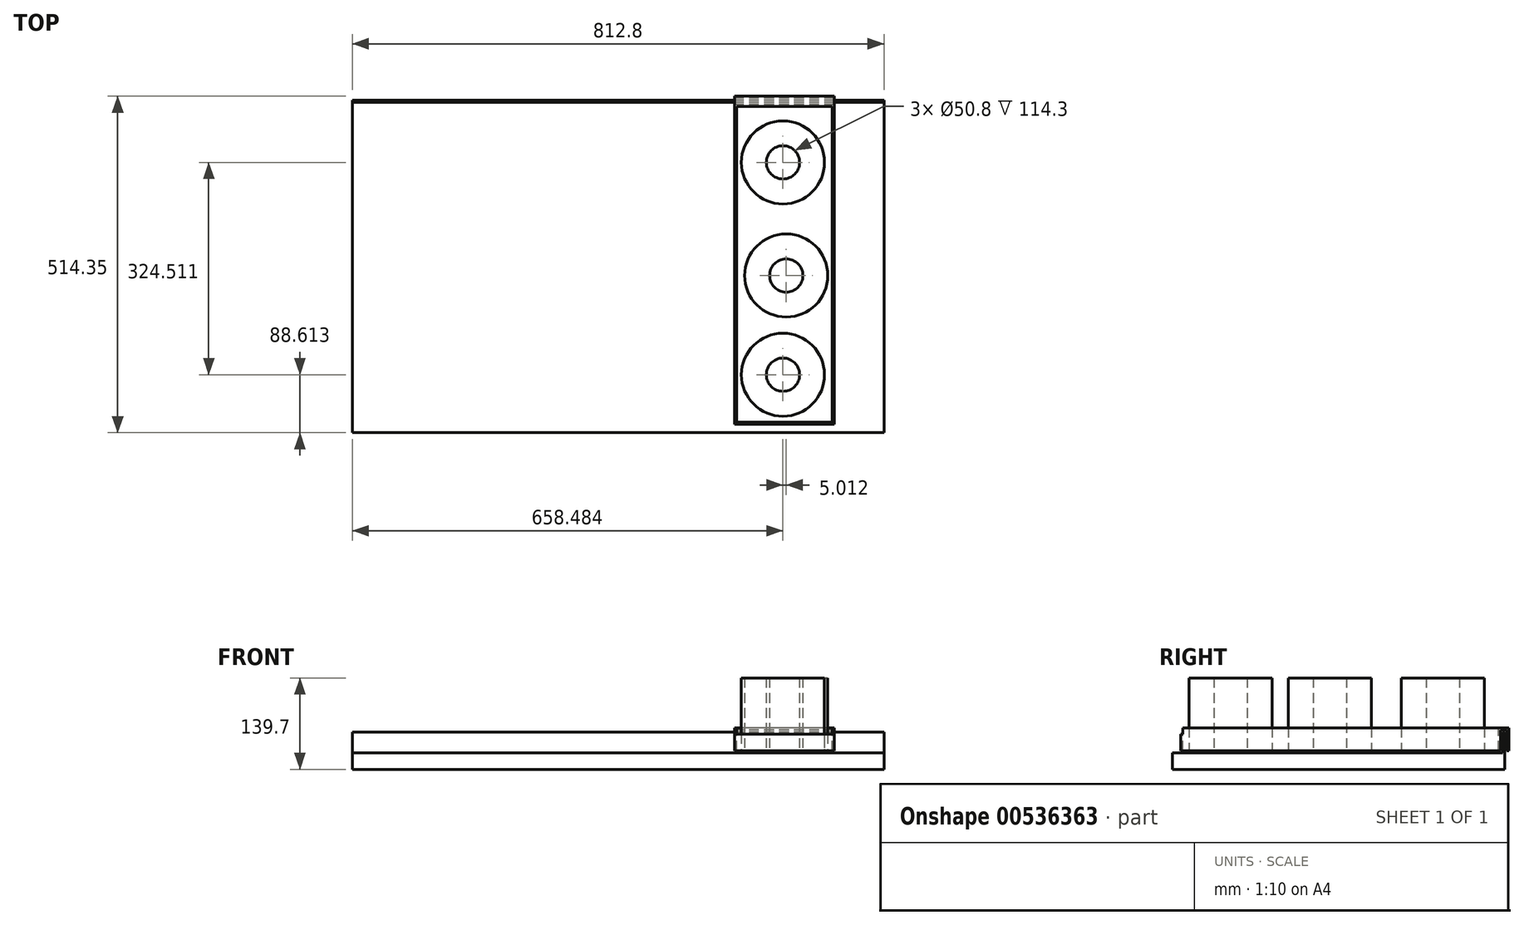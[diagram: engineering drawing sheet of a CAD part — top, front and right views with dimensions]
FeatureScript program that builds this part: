
annotation { "Feature Type Name" : "Feature", "Feature Type Description" : "" }
export const myFeature = defineFeature(function(context is Context, id is Id, definition is map)
    precondition{}
    {
        {
            var Q0;
            Q0=qCreatedBy(makeId("Top.planeOp"),FACE);
            var sketch = newSketch(context, id + "F0", { "sketchPlane" : qUnion([Q0])});
            skLineSegment(sketch, "E0.bottom", {"start": v(-406.4, 254) * mm, "end": v(406.4, 254) * mm});
            skLineSegment(sketch, "E0.top", {"start": v(-406.4, -254) * mm, "end": v(406.4, -254) * mm});
            skLineSegment(sketch, "E0.left", {"start": v(-406.4, 254) * mm, "end": v(-406.4, -254) * mm});
            skLineSegment(sketch, "E0.right", {"start": v(406.4, 254) * mm, "end": v(406.4, -254) * mm});
            skPoint(sketch, "E0.middle", {"position": v(0, 0) * mm});
            skSolve(sketch);
        }
        {
            var Q0;
            Q0 = qSketchRegion(id + "F0", true);
            extrude(context, id + "F1", {"entities" : qUnion([Q0]), "oppositeDirection" : true, "depth" : 25.4 * mm, "offsetDistance" : 25.4 * mm});
        }
        {
            var Q0;
            Q0=qCreatedBy(makeId("Right.planeOp"),FACE);
            var sketch = newSketch(context, id + "F2", { "sketchPlane" : qUnion([Q0])});
            skLineSegment(sketch, "E1.bottom", {"start": v(254, 0) * mm, "end": v(250.83, 0) * mm});
            skLineSegment(sketch, "E1.top", {"start": v(254, 31.75) * mm, "end": v(250.83, 31.75) * mm});
            skLineSegment(sketch, "E1.left", {"start": v(254, 0) * mm, "end": v(254, 31.75) * mm});
            skLineSegment(sketch, "E1.right", {"start": v(250.83, 0) * mm, "end": v(250.83, 31.75) * mm});
            skSolve(sketch);
        }
        {
            var Q0;
            Q0 = qSketchRegion(id + "F2", true);
            extrude(context, id + "F3", {"entities" : qUnion([Q0]), "operationType" : NewBodyOperationType.ADD, "endBound" : BoundingType.SYMMETRIC, "depth" : 812.8 * mm, "offsetDistance" : 25.4 * mm});
        }
        {
            var Q0;
            Q0=qCreatedBy(makeId("Right.planeOp"),FACE);
            cPlane(context, id + "F4", {"entities" : qUnion([Q0]), "cplaneType" : CPlaneType.OFFSET, "offset" : 254 * mm, "width" : 152.4 * mm, "height" : 152.4 * mm});
        }
        {
            var Q0;
            Q0=qCreatedBy(id+"F4.planeOp",FACE);
            var sketch = newSketch(context, id + "F5", { "sketchPlane" : qUnion([Q0])});
            skLineSegment(sketch, "E2", {"start": v(247.65, 3.18) * mm, "end": v(244.49, 3.18) * mm});
            skLineSegment(sketch, "E3", {"start": v(244.49, 3.18) * mm, "end": v(244.49, 38.1) * mm});
            skLineSegment(sketch, "E4", {"start": v(244.49, 38.1) * mm, "end": v(260.35, 38.1) * mm});
            skLineSegment(sketch, "E5", {"start": v(260.35, 38.1) * mm, "end": v(260.35, 3.17) * mm});
            skLineSegment(sketch, "E6", {"start": v(260.35, 3.17) * mm, "end": v(257.18, 3.17) * mm});
            skLineSegment(sketch, "E7", {"start": v(257.18, 3.17) * mm, "end": v(257.18, 34.92) * mm});
            skLineSegment(sketch, "E8", {"start": v(257.18, 34.92) * mm, "end": v(247.65, 34.92) * mm});
            skLineSegment(sketch, "E9", {"start": v(247.65, 34.92) * mm, "end": v(247.65, 3.18) * mm});
            skSolve(sketch);
        }
        {
            var Q0;
            Q0 = qSketchRegion(id + "F5", true);
            extrude(context, id + "F6", {"entities" : qUnion([Q0]), "endBound" : BoundingType.SYMMETRIC, "depth" : 152.4 * mm, "offsetDistance" : 25.4 * mm});
        }
        {
            var Q0;
            Q0=makeQuery(id+"F6.opExtrude","SWEPT_FACE",FACE,{"disambiguationData":[OSD([sQuery(id+"F5.wireOp",EDGE,"E3")])]});
            var sketch = newSketch(context, id + "F7", { "sketchPlane" : qUnion([Q0])});
            skLineSegment(sketch, "E10.bottom", {"start": v(177.8, 3.18) * mm, "end": v(180.98, 3.18) * mm});
            skLineSegment(sketch, "E10.top", {"start": v(177.8, 38.1) * mm, "end": v(180.98, 38.1) * mm});
            skLineSegment(sketch, "E10.left", {"start": v(177.8, 3.18) * mm, "end": v(177.8, 38.1) * mm});
            skLineSegment(sketch, "E10.right", {"start": v(180.98, 3.18) * mm, "end": v(180.98, 38.1) * mm});
            skLineSegment(sketch, "E11.bottom", {"start": v(330.2, 3.18) * mm, "end": v(327.03, 3.18) * mm});
            skLineSegment(sketch, "E11.top", {"start": v(330.2, 38.1) * mm, "end": v(327.03, 38.1) * mm});
            skLineSegment(sketch, "E11.left", {"start": v(330.2, 3.18) * mm, "end": v(330.2, 38.1) * mm});
            skLineSegment(sketch, "E11.right", {"start": v(327.03, 3.18) * mm, "end": v(327.03, 38.1) * mm});
            skSolve(sketch);
        }
        {
            var Q0;
            Q0 = qSketchRegion(id + "F7", true);
            extrude(context, id + "F8", {"entities" : qUnion([Q0]), "operationType" : NewBodyOperationType.ADD, "depth" : 482.6 * mm, "offsetDistance" : 25.4 * mm});
        }
        {
            var Q0;
            Q0=makeQuery(id+"F8.opExtrude","CAP_FACE",FACE,{"disambiguationData":[OSD([sQuery(id+"F7.wireOp",EDGE,"E10.bottom"),sQuery(id+"F7.wireOp",EDGE,"E10.top"),sQuery(id+"F7.wireOp",EDGE,"E10.left"),sQuery(id+"F7.wireOp",EDGE,"E10.right")])],"isStart":false});
            var sketch = newSketch(context, id + "F9", { "sketchPlane" : qUnion([Q0])});
            skLineSegment(sketch, "E12.bottom", {"start": v(177.8, 3.18) * mm, "end": v(330.2, 3.18) * mm});
            skLineSegment(sketch, "E12.top", {"start": v(177.8, 28.58) * mm, "end": v(330.2, 28.58) * mm});
            skLineSegment(sketch, "E12.left", {"start": v(177.8, 3.18) * mm, "end": v(177.8, 28.58) * mm});
            skLineSegment(sketch, "E12.right", {"start": v(330.2, 3.18) * mm, "end": v(330.2, 28.58) * mm});
            skSolve(sketch);
        }
        {
            var Q0;
            Q0 = qSketchRegion(id + "F9", true);
            extrude(context, id + "F10", {"entities" : qUnion([Q0]), "operationType" : NewBodyOperationType.ADD, "depth" : 3.17 * mm, "offsetDistance" : 25.4 * mm});
        }
        {
            var Q0;
            Q0=makeQuery(id+"F1.opExtrude","CAP_FACE",FACE,{"disambiguationData":[OSD([sQuery(id+"F0.wireOp",EDGE,"E0.bottom"),sQuery(id+"F0.wireOp",EDGE,"E0.top"),sQuery(id+"F0.wireOp",EDGE,"E0.left"),sQuery(id+"F0.wireOp",EDGE,"E0.right")])],"isStart":true});
            var sketch = newSketch(context, id + "F11", { "sketchPlane" : qUnion([Q0])});
            skCircle(sketch, "E13", {"center": v(252.08, 159.12) * mm, "radius": 63.5 * mm});
            skCircle(sketch, "E14", {"center": v(257.1, -13.78) * mm, "radius": 63.5 * mm});
            skCircle(sketch, "E15", {"center": v(257.1, -13.78) * mm, "radius": 25.4 * mm});
            skCircle(sketch, "E16", {"center": v(252.08, 159.12) * mm, "radius": 25.4 * mm});
            skCircle(sketch, "E17", {"center": v(252.08, -165.39) * mm, "radius": 63.5 * mm});
            skCircle(sketch, "E18", {"center": v(252.08, -165.39) * mm, "radius": 25.4 * mm});
            skSolve(sketch);
        }
        {
            var Q0;
            Q0 = qSketchRegion(id + "F11", true);
            extrude(context, id + "F12", {"entities" : qUnion([Q0]), "operationType" : NewBodyOperationType.ADD, "depth" : 114.3 * mm, "offsetDistance" : 25.4 * mm});
        }
    });
